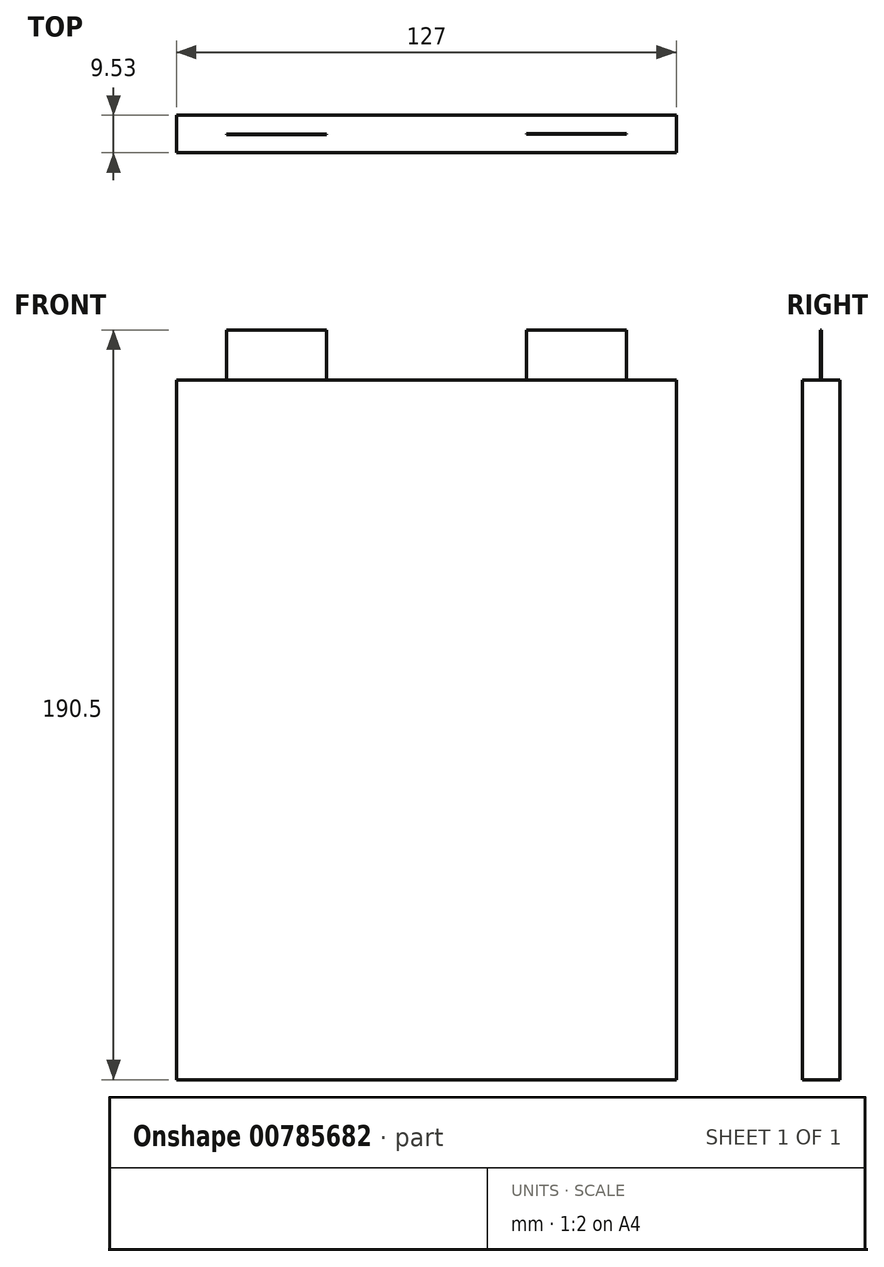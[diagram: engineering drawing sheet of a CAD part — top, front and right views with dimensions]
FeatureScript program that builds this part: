
annotation { "Feature Type Name" : "Feature", "Feature Type Description" : "" }
export const myFeature = defineFeature(function(context is Context, id is Id, definition is map)
    precondition{}
    {
        {
            var Q0;
            Q0=qCreatedBy(makeId("Front.planeOp"),FACE);
            var sketch = newSketch(context, id + "F0", { "sketchPlane" : qUnion([Q0])});
            skLineSegment(sketch, "E0.bottom", {"start": v(-63.5, 88.9) * mm, "end": v(63.5, 88.9) * mm});
            skLineSegment(sketch, "E0.top", {"start": v(-63.5, -88.9) * mm, "end": v(63.5, -88.9) * mm});
            skLineSegment(sketch, "E0.left", {"start": v(-63.5, 88.9) * mm, "end": v(-63.5, -88.9) * mm});
            skLineSegment(sketch, "E0.right", {"start": v(63.5, 88.9) * mm, "end": v(63.5, -88.9) * mm});
            skPoint(sketch, "E0.middle", {"position": v(0, 0) * mm});
            skSolve(sketch);
        }
        {
            var Q0;
            Q0 = qSketchRegion(id + "F0", true);
            extrude(context, id + "F1", {"entities" : qUnion([Q0]), "depth" : 9.52 * mm, "offsetDistance" : 25.4 * mm});
        }
        {
            var Q0;
            Q0=makeQuery(id+"F1.opExtrude","SWEPT_FACE",FACE,{"disambiguationData":[OSD([sQuery(id+"F0.wireOp",EDGE,"E0.bottom")])]});
            var sketch = newSketch(context, id + "F2", { "sketchPlane" : qUnion([Q0])});
            skLineSegment(sketch, "E1.bottom", {"start": v(50.8, -4.84) * mm, "end": v(25.4, -4.84) * mm});
            skLineSegment(sketch, "E1.top", {"start": v(50.8, -4.69) * mm, "end": v(25.4, -4.69) * mm});
            skLineSegment(sketch, "E1.left", {"start": v(50.8, -4.84) * mm, "end": v(50.8, -4.69) * mm});
            skLineSegment(sketch, "E1.right", {"start": v(25.4, -4.84) * mm, "end": v(25.4, -4.69) * mm});
            skPoint(sketch, "E1.middle", {"position": v(38.1, -4.76) * mm});
            skLineSegment(sketch, "E2.bottom", {"start": v(-25.4, -4.91) * mm, "end": v(-50.8, -4.91) * mm});
            skLineSegment(sketch, "E2.top", {"start": v(-25.4, -4.76) * mm, "end": v(-50.8, -4.76) * mm});
            skLineSegment(sketch, "E2.left", {"start": v(-25.4, -4.91) * mm, "end": v(-25.4, -4.76) * mm});
            skLineSegment(sketch, "E2.right", {"start": v(-50.8, -4.91) * mm, "end": v(-50.8, -4.76) * mm});
            skPoint(sketch, "E2.middle", {"position": v(-38.1, -4.84) * mm});
            skSolve(sketch);
        }
        {
            var Q0;
            Q0 = qSketchRegion(id + "F2", true);
            extrude(context, id + "F3", {"entities" : qUnion([Q0]), "operationType" : NewBodyOperationType.ADD, "depth" : 12.7 * mm, "offsetDistance" : 25.4 * mm});
        }
    });
